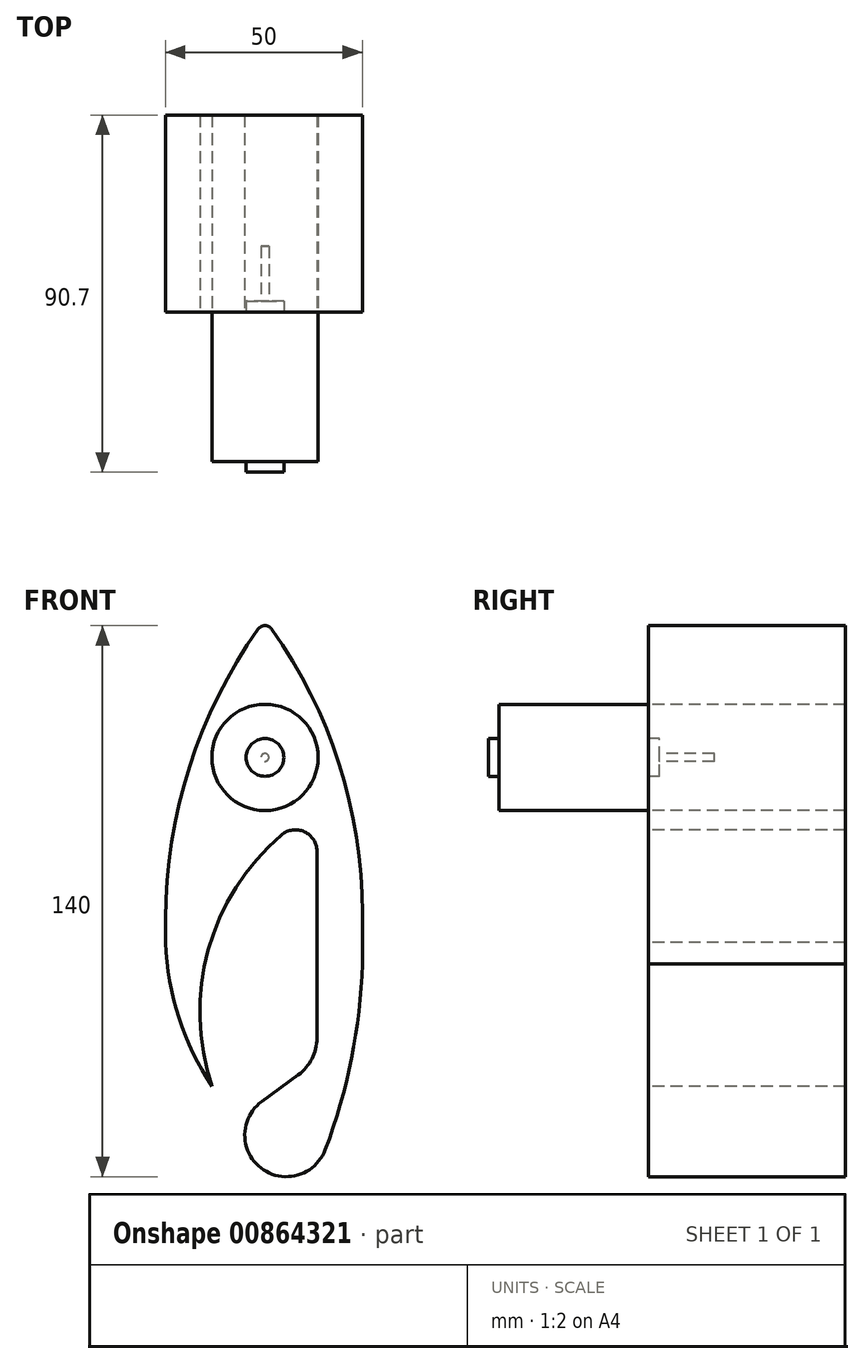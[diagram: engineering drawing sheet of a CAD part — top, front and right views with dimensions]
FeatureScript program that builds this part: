
annotation { "Feature Type Name" : "Feature", "Feature Type Description" : "" }
export const myFeature = defineFeature(function(context is Context, id is Id, definition is map)
    precondition{}
    {
        {
            var Q0;
            Q0=qCreatedBy(makeId("Top.planeOp"),FACE);
            var sketch = newSketch(context, id + "F0", { "sketchPlane" : qUnion([Q0])});
            skLineSegment(sketch, "E0", {"start": v(0, 0) * mm, "end": v(0, 57.4) * mm});
            skLineSegment(sketch, "E1", {"start": v(0, 57.4) * mm, "end": v(1, 57.4) * mm});
            skLineSegment(sketch, "E2", {"start": v(1, 57.4) * mm, "end": v(1, 43.4) * mm});
            skLineSegment(sketch, "E3", {"start": v(1, 43.4) * mm, "end": v(4.8, 43.4) * mm});
            skLineSegment(sketch, "E4", {"start": v(4.8, 43.4) * mm, "end": v(4.8, 40.7) * mm});
            skLineSegment(sketch, "E5", {"start": v(4.8, 40.7) * mm, "end": v(13.5, 40.7) * mm});
            skLineSegment(sketch, "E6", {"start": v(13.5, 40.7) * mm, "end": v(13.5, 2.7) * mm});
            skLineSegment(sketch, "E7", {"start": v(13.5, 2.7) * mm, "end": v(4.8, 2.7) * mm});
            skLineSegment(sketch, "E8", {"start": v(4.8, 2.7) * mm, "end": v(4.8, 0) * mm});
            skLineSegment(sketch, "E9", {"start": v(4.8, 0) * mm, "end": v(0, 0) * mm});
            skSolve(sketch);
        }
        {
            var Q0;
            Q0=makeQuery(id+"F0.imprint","IMPRINT",FACE,{"disambiguationData":[TD([[makeQuery(id+"F0.imprint","IMPRINT",EDGE,{"derivedFrom":sQuery(id+"F0.wireOp",EDGE,"E0")}),-1.0]])]});
            var Q1;
            Q1=sQuery(id+"F0.wireOp",EDGE,"E0");
            revolve(context, id + "F1", {"surfaceOperationType" : NewSurfaceOperationType.NEW, "entities" : qUnion([Q0]), "axis" : qUnion([Q1]), "revolveType" : RevolveType.FULL});
        }
        {
            var Q0;
            Q0=makeQuery(id+"F1.opRevolve","SWEPT_FACE",FACE,{"disambiguationData":[OSD([sQuery(id+"F0.wireOp",EDGE,"E5")])]});
            var sketch = newSketch(context, id + "F2", { "sketchPlane" : qUnion([Q0])});
            skLineSegment(sketch, "E10.bottom", {"start": v(-24.75, -106.52) * mm, "end": v(25.25, -106.52) * mm});
            skLineSegment(sketch, "E10.top", {"start": v(-24.75, 33.48) * mm, "end": v(25.25, 33.48) * mm});
            skLineSegment(sketch, "E10.left", {"start": v(-24.75, -106.52) * mm, "end": v(-24.75, 33.48) * mm});
            skLineSegment(sketch, "E10.right", {"start": v(25.25, -106.52) * mm, "end": v(25.25, 33.48) * mm});
            skPoint(sketch, "E10.middle", {"position": v(0.25, -36.52) * mm});
            skArc(sketch, "E11", {"start": v(25.25, -41.07) * mm, "mid": v(19.22, -2.4) * mm, "end": v(1.7, 32.6) * mm});
            skArc(sketch, "E12", {"start": v(1.7, 32.6) * mm, "mid": v(0, 33.48) * mm, "end": v(-1.7, 32.6) * mm});
            skArc(sketch, "E13", {"start": v(13.43, -83.61) * mm, "mid": v(14.42, -48.95) * mm, "end": v(-4.18, -19.7) * mm});
            skArc(sketch, "E14", {"start": v(-4.18, -19.7) * mm, "mid": v(-10.02, -18.89) * mm, "end": v(-13.2, -23.85) * mm});
            skLineSegment(sketch, "E15", {"start": v(-13.2, -23.85) * mm, "end": v(-13.2, -71.34) * mm});
            skArc(sketch, "E16", {"start": v(-13.2, -71.34) * mm, "mid": v(-11.94, -76.56) * mm, "end": v(-8.45, -80.66) * mm});
            skLineSegment(sketch, "E17", {"start": v(-8.45, -80.66) * mm, "end": v(0.8, -87.41) * mm});
            skArc(sketch, "E18", {"start": v(-15.3, -99.7) * mm, "mid": v(1, -104.35) * mm, "end": v(0.8, -87.41) * mm});
            skArc(sketch, "E19", {"start": v(-24.75, -52.48) * mm, "mid": v(-21.99, -76.48) * mm, "end": v(-15.3, -99.7) * mm});
            skArc(sketch, "E20", {"start": v(-1.7, 32.6) * mm, "mid": v(-18.85, -1.66) * mm, "end": v(-24.75, -39.5) * mm});
            skArc(sketch, "E21", {"start": v(13.43, -83.61) * mm, "mid": v(22.7, -63.27) * mm, "end": v(25.25, -41.07) * mm});
            skSolve(sketch);
        }
        {
            var Q0;
            {var subQ7=sQuery(id+"F2.wireOp",EDGE,"E11");Q0=makeQuery(id+"F2.imprint","IMPRINT",FACE,{"disambiguationData":[TD([[makeQuery(id+"F2.imprint","IMPRINT",EDGE,{"derivedFrom":subQ7}),1.0]])]});}
            extrude(context, id + "F3", {"entities" : qUnion([Q0]), "depth" : 50 * mm, "offsetDistance" : 25 * mm});
        }
    });
